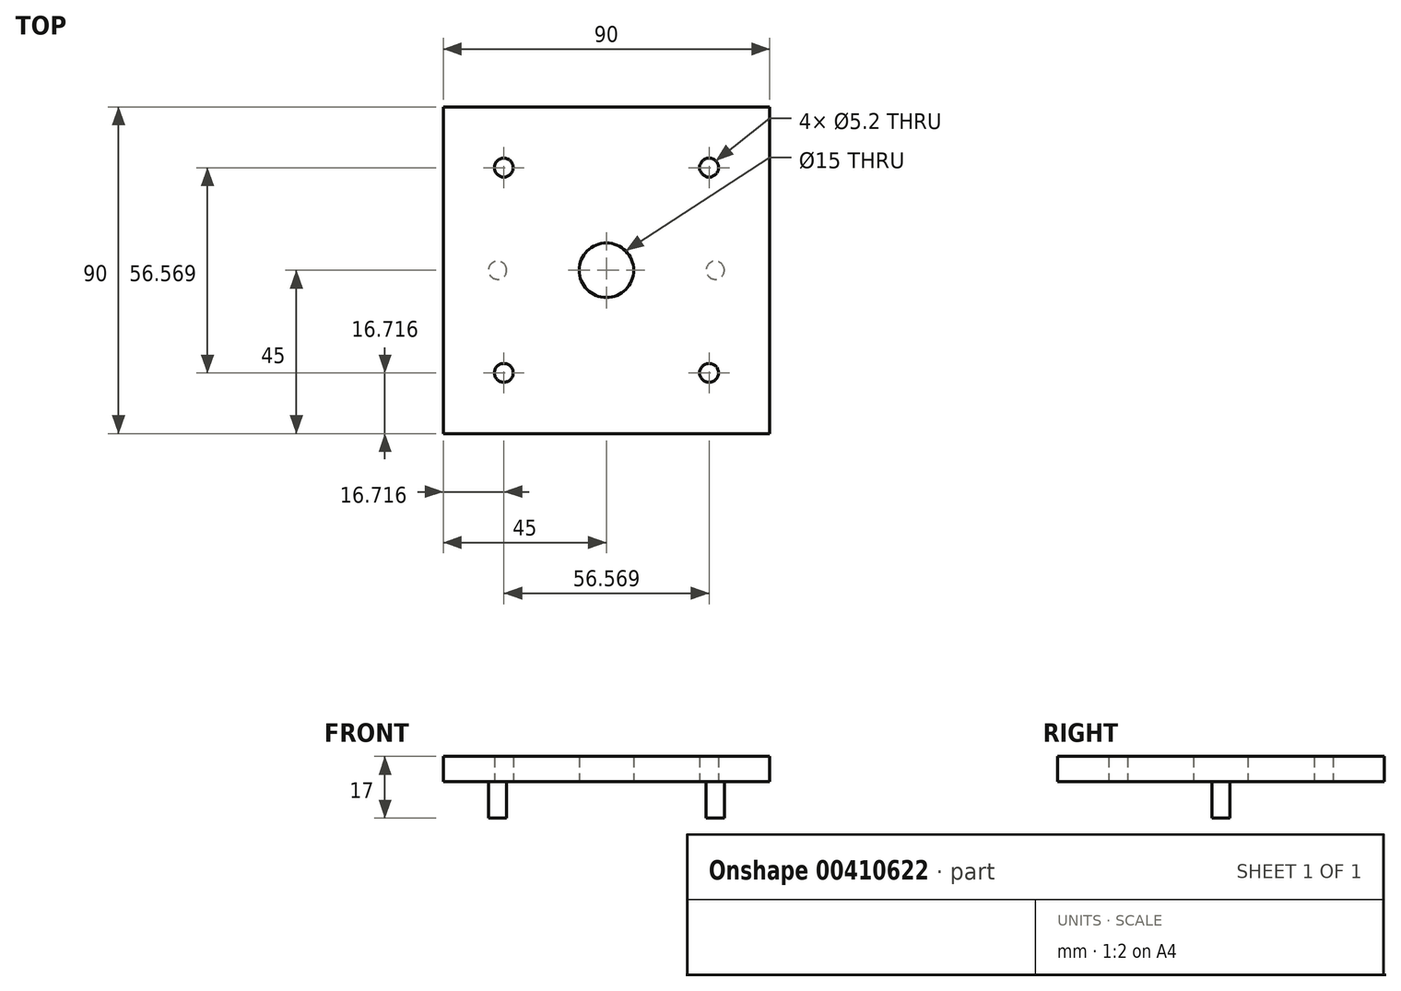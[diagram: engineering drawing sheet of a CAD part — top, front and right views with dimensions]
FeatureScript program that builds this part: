
annotation { "Feature Type Name" : "Feature", "Feature Type Description" : "" }
export const myFeature = defineFeature(function(context is Context, id is Id, definition is map)
    precondition{}
    {
        {
            var Q0;
            Q0=qCreatedBy(makeId("Top.planeOp"),FACE);
            var sketch = newSketch(context, id + "F0", { "sketchPlane" : qUnion([Q0])});
            skCircle(sketch, "E0", {"center": v(0, 0) * mm, "radius": 7.5 * mm});
            skCircle(sketch, "E1", {"center": v(-28.28, 28.28) * mm, "radius": 2.6 * mm});
            skCircle(sketch, "E2", {"center": v(28.28, 28.28) * mm, "radius": 2.6 * mm});
            skCircle(sketch, "E3", {"center": v(28.28, -28.28) * mm, "radius": 2.6 * mm});
            skCircle(sketch, "E4", {"center": v(-28.28, -28.28) * mm, "radius": 2.6 * mm});
            skCircle(sketch, "E5", {"center": v(-30, 0) * mm, "radius": 2.5 * mm});
            skCircle(sketch, "E6", {"center": v(30, 0) * mm, "radius": 2.5 * mm});
            skLineSegment(sketch, "E7.0", {"start": v(-28.28, -28.28) * mm, "end": v(0, 0) * mm, "construction": true});
            skLineSegment(sketch, "E8.0", {"start": v(0, 0) * mm, "end": v(28.28, 28.28) * mm, "construction": true});
            skLineSegment(sketch, "E9.0", {"start": v(28.28, -28.28) * mm, "end": v(-28.28, 28.28) * mm, "construction": true});
            skLineSegment(sketch, "E10.bottom", {"start": v(45, -45) * mm, "end": v(-45, -45) * mm});
            skLineSegment(sketch, "E10.top", {"start": v(45, 45) * mm, "end": v(-45, 45) * mm});
            skLineSegment(sketch, "E10.left", {"start": v(45, -45) * mm, "end": v(45, 45) * mm});
            skLineSegment(sketch, "E10.right", {"start": v(-45, -45) * mm, "end": v(-45, 45) * mm});
            skSolve(sketch);
        }
        {
            var Q0;
            Q0=makeQuery(id+"F0.imprint","IMPRINT",FACE,{"disambiguationData":[TD([[makeQuery(id+"F0.imprint","IMPRINT",EDGE,{"derivedFrom":sQuery(id+"F0.wireOp",EDGE,"E5")}),1.0]])]});
            var Q1;
            Q1=makeQuery(id+"F0.imprint","IMPRINT",FACE,{"disambiguationData":[TD([[makeQuery(id+"F0.imprint","IMPRINT",EDGE,{"derivedFrom":sQuery(id+"F0.wireOp",EDGE,"E6")}),1.0]])]});
            var Q2;
            Q2=makeQuery(id+"F0.imprint","IMPRINT",FACE,{"disambiguationData":[TD([[makeQuery(id+"F0.imprint","IMPRINT",EDGE,{"derivedFrom":sQuery(id+"F0.wireOp",EDGE,"E0")}),-1.0]])]});
            extrude(context, id + "F1", {"entities" : qUnion([Q0, Q1, Q2]), "depth" : 7 * mm});
        }
        {
            var Q0;
            Q0=makeQuery(id+"F0.imprint","IMPRINT",FACE,{"disambiguationData":[TD([[makeQuery(id+"F0.imprint","IMPRINT",EDGE,{"derivedFrom":sQuery(id+"F0.wireOp",EDGE,"8QngJfBw-EGaV-BhHd-0f6p-3G83t4KiV26R")}),1.0]])]});
            var Q1;
            Q1=makeQuery(id+"F0.imprint","IMPRINT",FACE,{"disambiguationData":[TD([[makeQuery(id+"F0.imprint","IMPRINT",EDGE,{"derivedFrom":sQuery(id+"F0.wireOp",EDGE,"E6")}),1.0]])]});
            var Q2;
            Q2=makeQuery(id+"F0.imprint","IMPRINT",FACE,{"disambiguationData":[TD([[makeQuery(id+"F0.imprint","IMPRINT",EDGE,{"derivedFrom":sQuery(id+"F0.wireOp",EDGE,"E5")}),1.0]])]});
            extrude(context, id + "F2", {"entities" : qUnion([Q0, Q1, Q2]), "operationType" : NewBodyOperationType.ADD, "oppositeDirection" : true, "depth" : 10 * mm});
        }
    });
